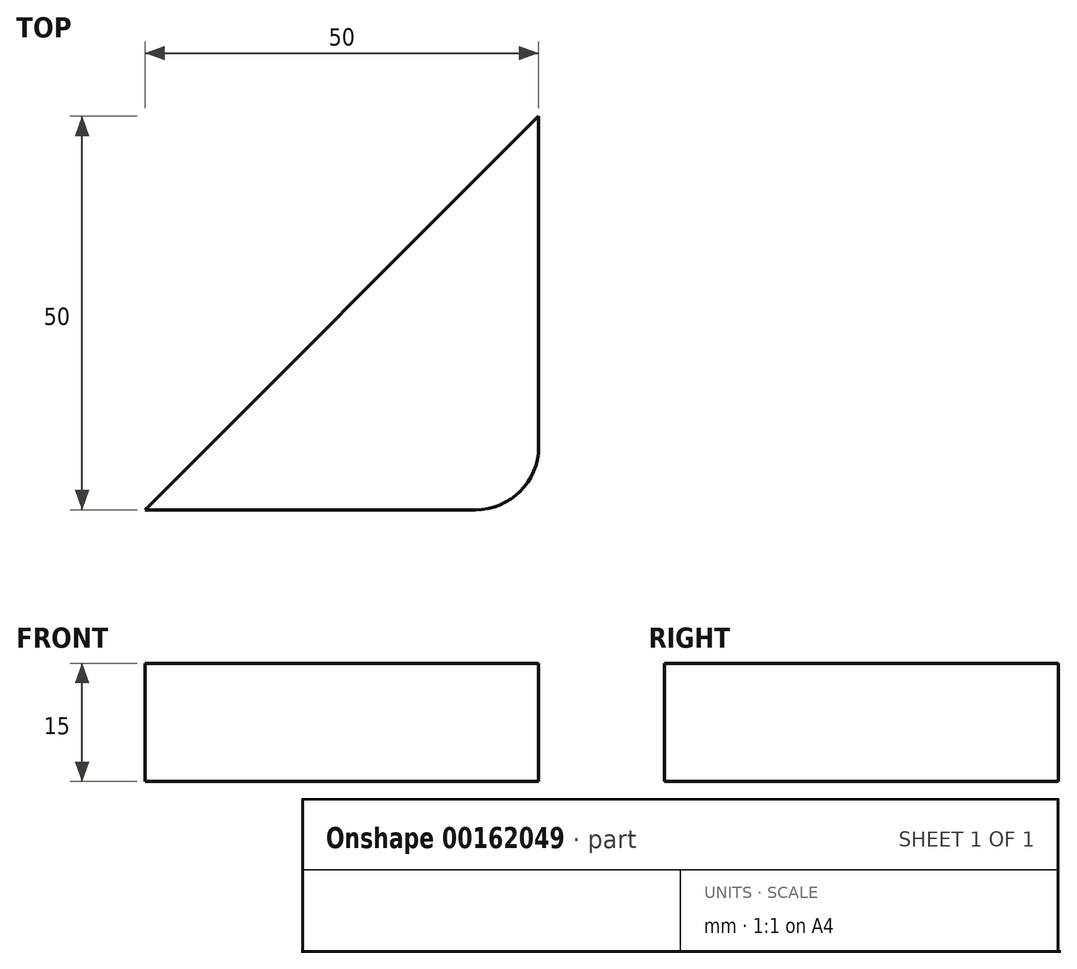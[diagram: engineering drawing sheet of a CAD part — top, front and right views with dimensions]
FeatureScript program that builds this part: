
annotation { "Feature Type Name" : "Feature", "Feature Type Description" : "" }
export const myFeature = defineFeature(function(context is Context, id is Id, definition is map)
    precondition{}
    {
        {
            var Q0;
            Q0=qCreatedBy(makeId("Top.planeOp"),FACE);
            var sketch = newSketch(context, id + "F0", { "sketchPlane" : qUnion([Q0])});
            skLineSegment(sketch, "E0", {"start": v(-0.7, -5.61) * mm, "end": v(41.3, -5.61) * mm});
            skLineSegment(sketch, "E1", {"start": v(49.3, 2.39) * mm, "end": v(49.3, 44.39) * mm});
            skLineSegment(sketch, "E2", {"start": v(-0.7, -5.61) * mm, "end": v(49.3, 44.39) * mm});
            skPoint(sketch, "E3.visualSharp", {"position": v(49.3, -5.61) * mm});
            skArc(sketch, "E3.filletArc", {"start": v(41.3, -5.61) * mm, "mid": v(46.96, -3.27) * mm, "end": v(49.3, 2.39) * mm});
            skSolve(sketch);
        }
        {
            var Q0;
            Q0=makeQuery(id+"F0.imprint","IMPRINT",FACE,{"disambiguationData":[TD([[makeQuery(id+"F0.imprint","IMPRINT",EDGE,{"derivedFrom":sQuery(id+"F0.wireOp",EDGE,"E0")}),1.0]])]});
            extrude(context, id + "F1", {"entities" : qUnion([Q0]), "depth" : 15 * mm});
        }
    });
